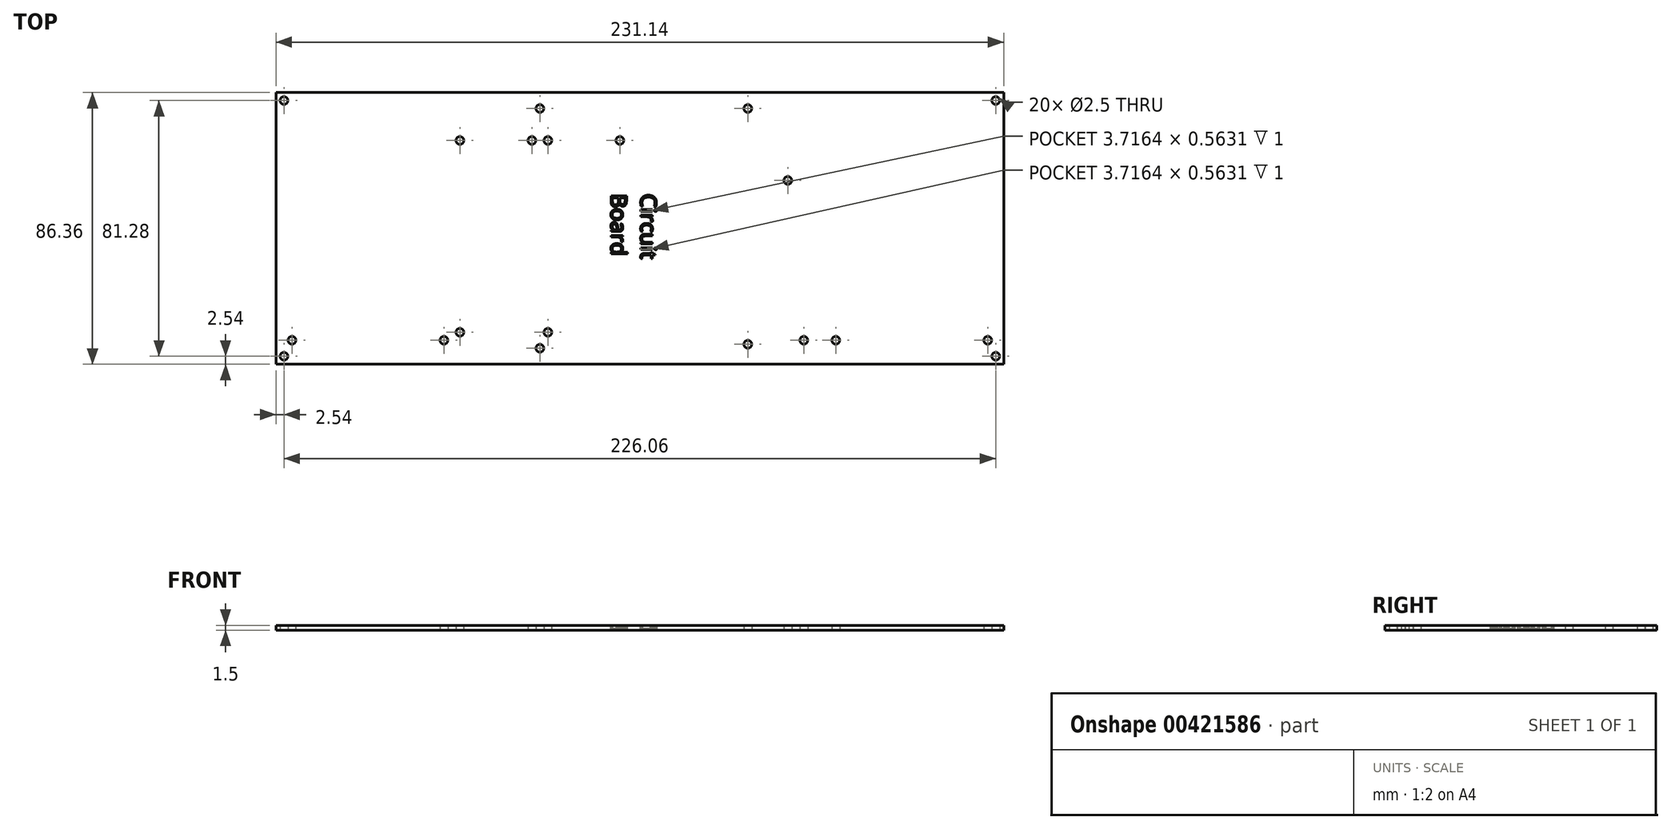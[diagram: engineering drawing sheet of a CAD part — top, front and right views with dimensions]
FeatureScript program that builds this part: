
annotation { "Feature Type Name" : "Feature", "Feature Type Description" : "" }
export const myFeature = defineFeature(function(context is Context, id is Id, definition is map)
    precondition{}
    {
        {
            var Q0;
            Q0=qCreatedBy(makeId("Top.planeOp"),FACE);
            var sketch = newSketch(context, id + "F0", { "sketchPlane" : qUnion([Q0])});
            skLineSegment(sketch, "E0.bottom", {"start": v(115.57, 43.18) * mm, "end": v(-115.57, 43.18) * mm});
            skLineSegment(sketch, "E0.top", {"start": v(115.57, -43.18) * mm, "end": v(-115.57, -43.18) * mm});
            skLineSegment(sketch, "E0.left", {"start": v(115.57, 43.18) * mm, "end": v(115.57, -43.18) * mm});
            skLineSegment(sketch, "E0.right", {"start": v(-115.57, 43.18) * mm, "end": v(-115.57, -43.18) * mm});
            skCircle(sketch, "E1", {"center": v(-113.03, 40.64) * mm, "radius": 1.25 * mm});
            skCircle(sketch, "E2", {"center": v(-31.75, 38.1) * mm, "radius": 1.25 * mm});
            skCircle(sketch, "E3.MirrorC", {"center": v(113.03, 40.64) * mm, "radius": 1.25 * mm});
            skCircle(sketch, "E4.MirrorC", {"center": v(34.29, 38.1) * mm, "radius": 1.25 * mm});
            skCircle(sketch, "E5.MirrorC", {"center": v(113.03, -40.64) * mm, "radius": 1.25 * mm});
            skCircle(sketch, "E6.MirrorC", {"center": v(-31.75, -38.1) * mm, "radius": 1.25 * mm});
            skCircle(sketch, "E7.MirrorC", {"center": v(-113.03, -40.64) * mm, "radius": 1.25 * mm});
            skCircle(sketch, "E8", {"center": v(34.3, -36.83) * mm, "radius": 1.25 * mm});
            skCircle(sketch, "E9", {"center": v(-110.49, -35.56) * mm, "radius": 1.25 * mm});
            skCircle(sketch, "E10", {"center": v(-62.23, -35.56) * mm, "radius": 1.25 * mm});
            skCircle(sketch, "E11", {"center": v(-57.15, 27.94) * mm, "radius": 1.25 * mm});
            skCircle(sketch, "E12", {"center": v(-57.15, -33.02) * mm, "radius": 1.25 * mm});
            skCircle(sketch, "E13", {"center": v(52.07, -35.56) * mm, "radius": 1.25 * mm});
            skCircle(sketch, "E14", {"center": v(47, 15.24) * mm, "radius": 1.25 * mm});
            skCircle(sketch, "E15", {"center": v(62.23, -35.56) * mm, "radius": 1.25 * mm});
            skCircle(sketch, "E16", {"center": v(110.5, -35.56) * mm, "radius": 1.25 * mm});
            skCircle(sketch, "E17", {"center": v(-29.2, -33.02) * mm, "radius": 1.25 * mm});
            skCircle(sketch, "E18", {"center": v(-34.29, 27.94) * mm, "radius": 1.25 * mm});
            skCircle(sketch, "E19", {"center": v(-6.35, 27.94) * mm, "radius": 1.25 * mm});
            skCircle(sketch, "E20", {"center": v(-29.2, 27.94) * mm, "radius": 1.25 * mm});
            skSolve(sketch);
        }
        {
            var Q0;
            Q0=makeQuery(id+"F0.imprint","IMPRINT",FACE,{"disambiguationData":[TD([[makeQuery(id+"F0.imprint","IMPRINT",EDGE,{"derivedFrom":sQuery(id+"F0.wireOp",EDGE,"E0.bottom")}),1.0]])]});
            extrude(context, id + "F1", {"entities" : qUnion([Q0]), "depth" : 1.5 * mm, "offsetDistance" : 25 * mm});
        }
        {
            var Q0;
            Q0=makeQuery(id+"F1.opExtrude","CAP_FACE",FACE,{"disambiguationData":[OSD([sQuery(id+"F0.wireOp",EDGE,"E0.bottom"),sQuery(id+"F0.wireOp",EDGE,"E0.top"),sQuery(id+"F0.wireOp",EDGE,"E0.left"),sQuery(id+"F0.wireOp",EDGE,"E0.right"),sQuery(id+"F0.wireOp",EDGE,"E1"),sQuery(id+"F0.wireOp",EDGE,"E2"),sQuery(id+"F0.wireOp",EDGE,"E3.MirrorC"),sQuery(id+"F0.wireOp",EDGE,"E4.MirrorC"),sQuery(id+"F0.wireOp",EDGE,"E5.MirrorC"),sQuery(id+"F0.wireOp",EDGE,"E6.MirrorC"),sQuery(id+"F0.wireOp",EDGE,"E7.MirrorC"),sQuery(id+"F0.wireOp",EDGE,"E8")])],"isStart":false});
            cPlane(context, id + "F2", {"entities" : qUnion([Q0]), "cplaneType" : CPlaneType.OFFSET, "offset" : 0 * mm, "width" : 150 * mm, "height" : 150 * mm});
        }
        {
            var Q0;
            Q0=qCreatedBy(id+"F2.planeOp",FACE);
            var sketch = newSketch(context, id + "F3", { "sketchPlane" : qUnion([Q0])});
            skText(sketch, "E21", { "text": "Circuit \nBoard\n", "fontName": "OpenSans-Regular.ttf"});
            const initialGuessF3  = {"E21": [0.00028, 0.01096, 0, -1, 0.005]};
            skSetInitialGuess(sketch, initialGuessF3);
            skSolve(sketch);
        }
        {
            var Q0;
            Q0 = qSketchRegion(id + "F3", true);
            extrude(context, id + "F4", {"entities" : qUnion([Q0]), "operationType" : NewBodyOperationType.REMOVE, "oppositeDirection" : true, "depth" : 1 * mm, "offsetDistance" : 25 * mm});
        }
    });
